# Revit family: Geberit kumanda kapağı Alpha50, 2 kademeli deşarj için_PRO_168883
name_source: partatom
category: Furniture
revit_build: Autodesk Revit 2018 (Build: 20190510_1515(x64)
units: mm (PartAtom-declared; Revit-internal decimal feet)

## family parameters
Always vertical = Yes
Cut with Voids When Loaded = No
OmniClass Number = 23.40.20.21
OmniClass Title = Toilet and Bath Specialties
Room Calculation Point = Yes
Shared = No
Work Plane-Based = No

## types (2) — shared parameters
115060_0_view = Yes
Application purposes = Geberit Alpha gömme rezervuarlarda deşarj tetiklemesi için
Application range = Furniture
B = 21.3 cm
BIM Content Version = GEB MG 1.2
BIM Content revision date = 2020.05.18
Brand = Geberit
CW Connection = Yes
Characteristics = Üstten veya önden basmalı
Description = Geberit kumanda kapağı Alpha50, 2 kademeli deşarj için
GEB_culture = tr-TR
GEB_generic_description = GBC
GEB_generic_manufacturer = generic
GEB_pimversion = 22.02.12
GEB_processing_type = T
GEB_reference = PRO_168883
GEB_translations = {"ATT_10673":"EAN code basic data","ATT_10931":"B","ATT_10951":"H","ATT_380239":"T","ATT_459792":"Renk / Yüzey","applicationPurposes":"Application purposes","application_range":"Application range","brandName":"Brand","characteristics":"Characteristics","content_creator":"BIM Content creator","content_date_changed":"BIM Content revision date","content_version":"BIM Content Version","key 1000":"Article number key","name":"Name","productBrand":"Product brand","scopeOfDelivery":"Scope of delivery","type":"Type","fixed_material":"Main material"}
H = 14.2 cm
HW Connection = No
IfcDescription = Geberit kumanda kapağı Alpha50, 2 kademeli deşarj için
IfcExportAs = IfcUnitaryControlElement
IfcExportType = CONTROLPANEL
LOD300 = No
LOD400 = Yes
Main material = Geberit, Plastic, Opaque white
Manufacturer = Geberit
Model = Alpha50 (Alpha50)
Name = Geberit kumanda kapağı Alpha50, 2 kademeli deşarj için
Scope of delivery = 2 basma çubuğu
Sabitleme malzemesi
T = 1.5 cm
Type = Alpha50 (Alpha50)
Vent Connection = No
Waste Connection = Yes

## per-type parameters (varying)
| type | Article number key | EAN code basic data | Renk / Yüzey |
| 115.060.DW.1 Geberit kumanda kapağı Alpha50, 2 kademeli deşarj için | 115.060.DW.1 | 4025416351290 | Siyah RAL 9005 |
| 115.060.11.1 Geberit kumanda kapağı Alpha50, 2 kademeli deşarj için | 115.060.11.1 | 4025416349662 | Beyaz |

## geometry (parser evidence)
native form markers: Blend x8, Sweep x8
no freeform markers — native parametric forms only
